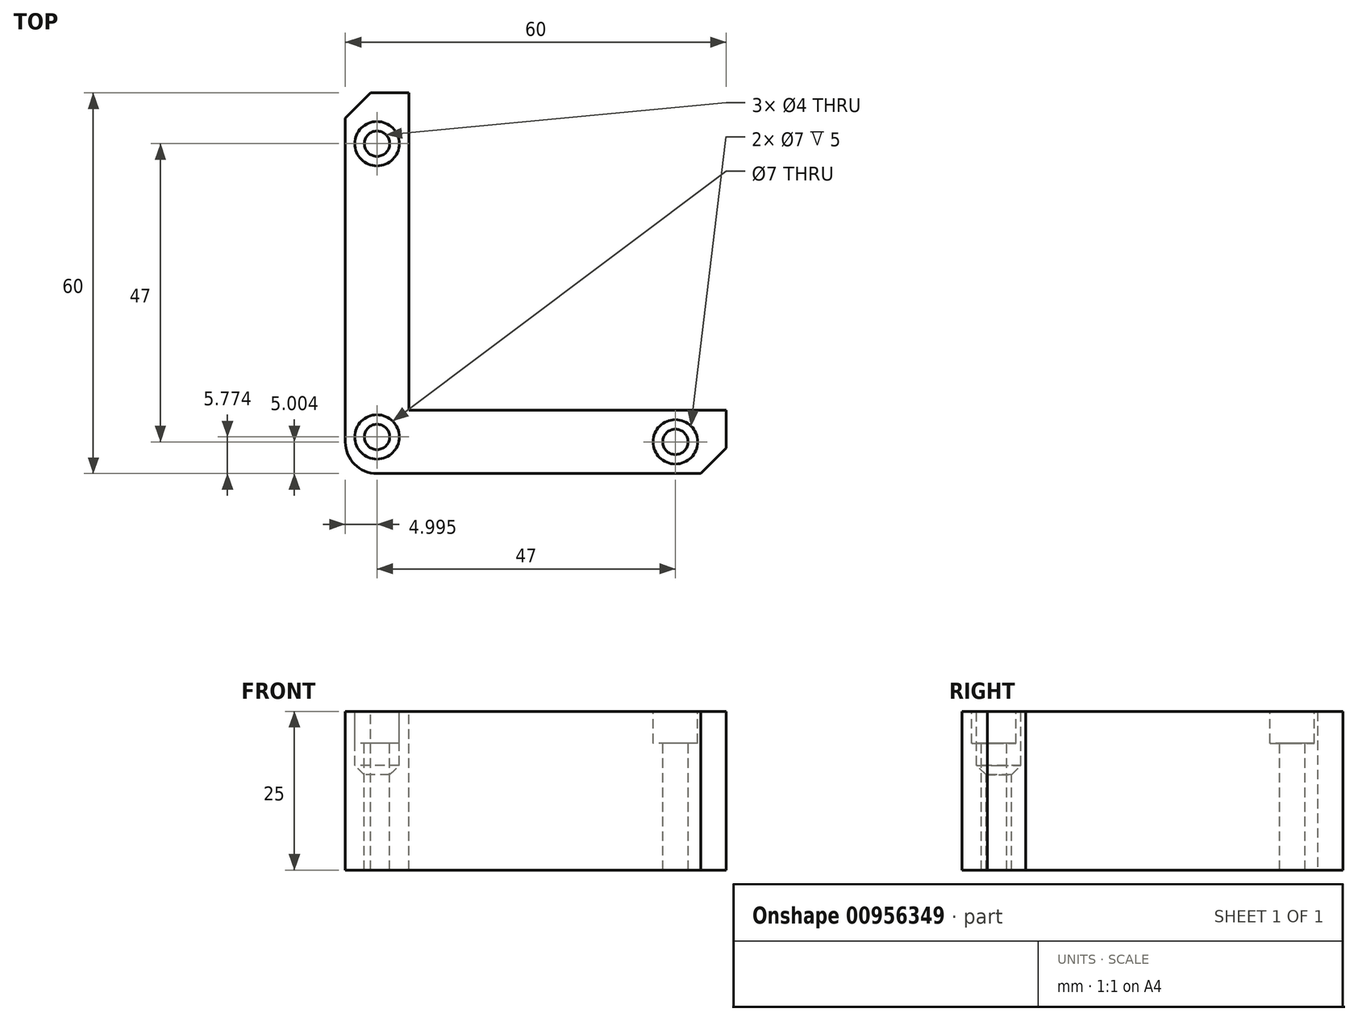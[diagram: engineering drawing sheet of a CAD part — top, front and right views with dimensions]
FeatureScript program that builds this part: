
annotation { "Feature Type Name" : "Feature", "Feature Type Description" : "" }
export const myFeature = defineFeature(function(context is Context, id is Id, definition is map)
    precondition{}
    {
        {
            var Q0;
            Q0=qCreatedBy(makeId("Top.planeOp"),FACE);
            var sketch = newSketch(context, id + "F0", { "sketchPlane" : qUnion([Q0])});
            skLineSegment(sketch, "E0.bottom", {"start": v(-26.92, 32.04) * mm, "end": v(33.08, 32.04) * mm});
            skLineSegment(sketch, "E0.top", {"start": v(-26.92, -27.96) * mm, "end": v(33.08, -27.96) * mm});
            skLineSegment(sketch, "E0.left", {"start": v(-26.92, 32.04) * mm, "end": v(-26.92, -27.96) * mm});
            skLineSegment(sketch, "E0.right", {"start": v(33.08, 32.04) * mm, "end": v(33.08, -27.96) * mm});
            skSolve(sketch);
        }
        {
            var Q0;
            Q0 = qSketchRegion(id + "F0", true);
            extrude(context, id + "F1", {"entities" : qUnion([Q0]), "depth" : 25 * mm, "offsetDistance" : 25 * mm});
        }
        {
            var Q0;
            Q0=makeQuery(id+"F1.opExtrude","CAP_FACE",FACE,{"disambiguationData":[OSD([sQuery(id+"F0.wireOp",EDGE,"E0.bottom"),sQuery(id+"F0.wireOp",EDGE,"E0.top"),sQuery(id+"F0.wireOp",EDGE,"E0.left"),sQuery(id+"F0.wireOp",EDGE,"E0.right")])],"isStart":false});
            var sketch = newSketch(context, id + "F2", { "sketchPlane" : qUnion([Q0])});
            skLineSegment(sketch, "E1.bottom", {"start": v(-16.92, 32.04) * mm, "end": v(33.08, 32.04) * mm});
            skLineSegment(sketch, "E1.top", {"start": v(-16.92, -17.96) * mm, "end": v(33.08, -17.96) * mm});
            skLineSegment(sketch, "E1.left", {"start": v(-16.92, 32.04) * mm, "end": v(-16.92, -17.96) * mm});
            skLineSegment(sketch, "E1.right", {"start": v(33.08, 32.04) * mm, "end": v(33.08, -17.96) * mm});
            skSolve(sketch);
        }
        {
            var Q0;
            Q0 = qSketchRegion(id + "F2", true);
            extrude(context, id + "F3", {"entities" : qUnion([Q0]), "operationType" : NewBodyOperationType.REMOVE, "oppositeDirection" : true, "depth" : 25 * mm, "offsetDistance" : 25 * mm});
        }
        {
            var Q0;
            Q0=makeQuery(id+"F1.opExtrude","SWEPT_EDGE",EDGE,{"disambiguationData":[OSD([sQuery(id+"F0.wireOp",EDGE,"E0.top"),sQuery(id+"F0.wireOp",EDGE,"E0.left")])]});
            fillet(context, id + "F4", {"entities" : qUnion([Q0]), "radius" : 5 * mm, "tangentPropagation" : true, "allowEdgeOverflow" : false});
        }
        {
            var Q0;
            Q0=makeQuery(id+"F1.opExtrude","CAP_FACE",FACE,{"disambiguationData":[OSD([sQuery(id+"F0.wireOp",EDGE,"E0.bottom"),sQuery(id+"F0.wireOp",EDGE,"E0.top"),sQuery(id+"F0.wireOp",EDGE,"E0.left"),sQuery(id+"F0.wireOp",EDGE,"E0.right")])],"isStart":false});
            var sketch = newSketch(context, id + "F5", { "sketchPlane" : qUnion([Q0])});
            skCircle(sketch, "E2", {"center": v(-21.92, 24.04) * mm, "radius": 2 * mm});
            skCircle(sketch, "E3", {"center": v(-21.92, -22.19) * mm, "radius": 2 * mm});
            skCircle(sketch, "E4", {"center": v(25.08, -22.96) * mm, "radius": 2 * mm});
            skSolve(sketch);
        }
        {
            var Q0;
            Q0 = qSketchRegion(id + "F5", true);
            extrude(context, id + "F6", {"entities" : qUnion([Q0]), "operationType" : NewBodyOperationType.REMOVE, "oppositeDirection" : true, "depth" : 28 * mm, "offsetDistance" : 25 * mm});
        }
        {
            var Q0;
            Q0=makeQuery(id+"F1.opExtrude","CAP_FACE",FACE,{"disambiguationData":[OSD([sQuery(id+"F0.wireOp",EDGE,"E0.bottom"),sQuery(id+"F0.wireOp",EDGE,"E0.top"),sQuery(id+"F0.wireOp",EDGE,"E0.left"),sQuery(id+"F0.wireOp",EDGE,"E0.right")])],"isStart":false});
            var sketch = newSketch(context, id + "F7", { "sketchPlane" : qUnion([Q0])});
            skCircle(sketch, "E5", {"center": v(-21.92, 24.04) * mm, "radius": 3.5 * mm});
            skCircle(sketch, "E6", {"center": v(25.08, -22.96) * mm, "radius": 3.5 * mm});
            skCircle(sketch, "E7", {"center": v(-21.92, -22.19) * mm, "radius": 3.5 * mm});
            skSolve(sketch);
        }
        {
            var Q0;
            Q0 = qSketchRegion(id + "F7", true);
            extrude(context, id + "F8", {"entities" : qUnion([Q0]), "operationType" : NewBodyOperationType.REMOVE, "oppositeDirection" : true, "depth" : 5 * mm, "offsetDistance" : 25 * mm});
        }
        {
            var Q0;
            Q0=makeQuery(id+"F8.boolean.opBoolean","INTERSECT",EDGE,{"derivedFrom":[makeQuery(id+"F6.boolean.opBoolean","COPY",FACE,{"derivedFrom":makeQuery(id+"F6.opExtrude","SWEPT_FACE",FACE,{"disambiguationData":[OSD([sQuery(id+"F5.wireOp",EDGE,"E3")])]})}),makeQuery(id+"F8.opExtrude","CAP_FACE",FACE,{"disambiguationData":[OSD([sQuery(id+"F7.wireOp",EDGE,"E7")])],"isStart":false})]});
            chamfer(context, id + "F9", {"entities" : qUnion([Q0]), "width" : 5 * mm, "tangentPropagation" : true});
        }
        {
            var Q0;
            Q0=makeQuery(id+"F1.opExtrude","SWEPT_EDGE",EDGE,{"disambiguationData":[OSD([sQuery(id+"F0.wireOp",EDGE,"E0.bottom"),sQuery(id+"F0.wireOp",EDGE,"E0.left")])]});
            var Q1;
            Q1=makeQuery(id+"F1.opExtrude","SWEPT_EDGE",EDGE,{"disambiguationData":[OSD([sQuery(id+"F0.wireOp",EDGE,"E0.top"),sQuery(id+"F0.wireOp",EDGE,"E0.right")])]});
            chamfer(context, id + "F10", {"entities" : qUnion([Q0, Q1]), "width" : 4 * mm, "tangentPropagation" : true});
        }
    });
